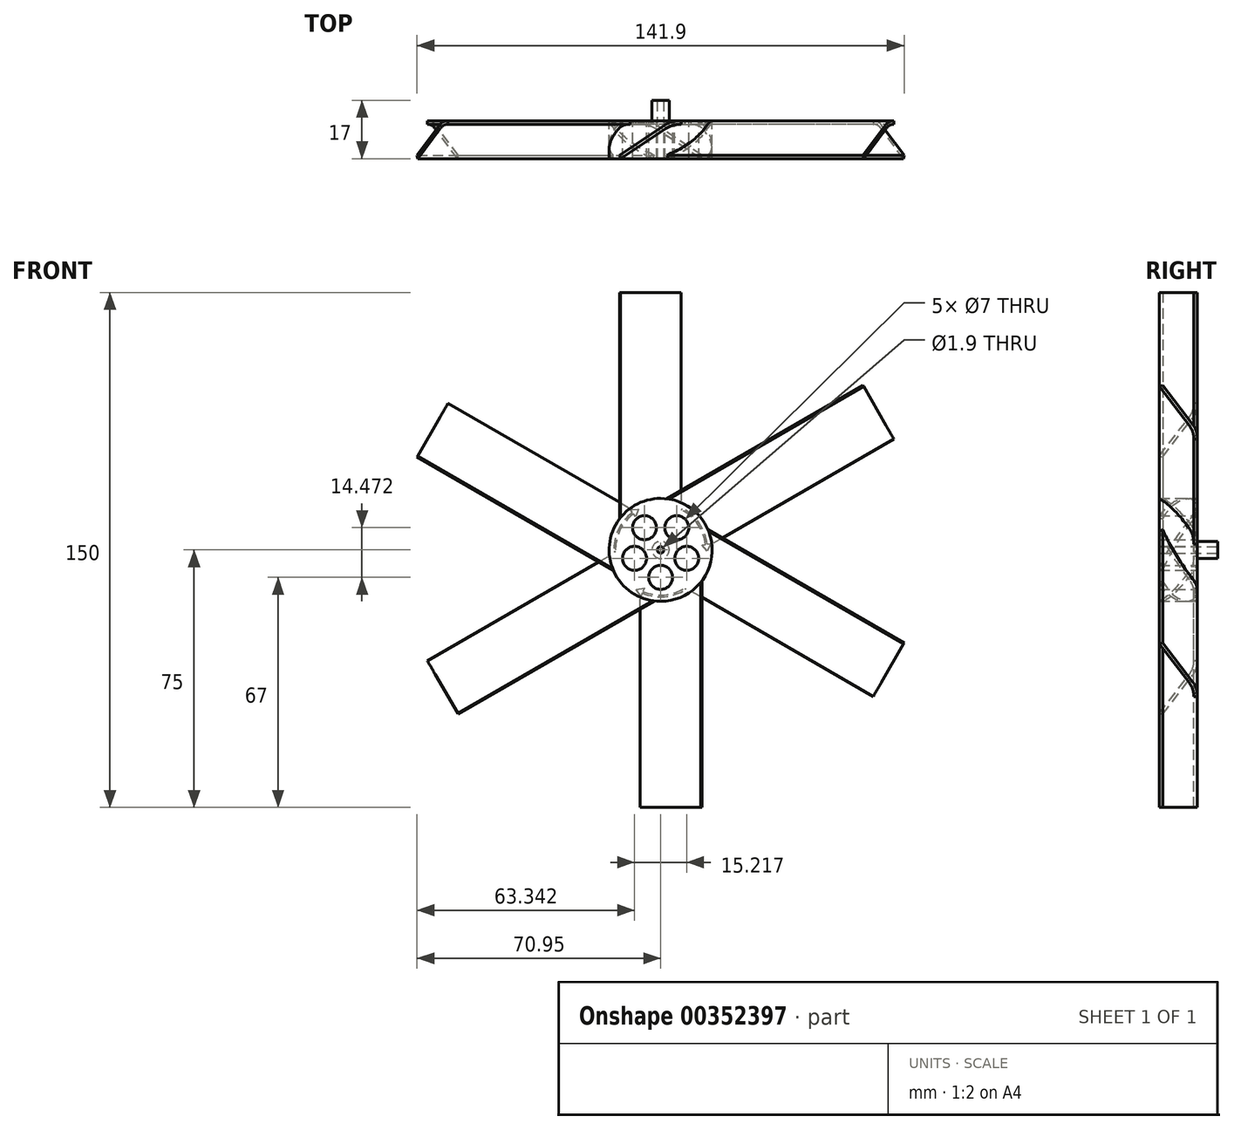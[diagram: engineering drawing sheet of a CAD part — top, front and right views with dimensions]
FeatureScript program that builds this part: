
annotation { "Feature Type Name" : "Feature", "Feature Type Description" : "" }
export const myFeature = defineFeature(function(context is Context, id is Id, definition is map)
    precondition{}
    {
        {
            var Q0;
            Q0=qCreatedBy(makeId("Top.planeOp"),FACE);
            var sketch = newSketch(context, id + "F0", { "sketchPlane" : qUnion([Q0])});
            skLineSegment(sketch, "E0", {"start": v(-3, 0) * mm, "end": v(12, 0) * mm, "construction": true});
            skLineSegment(sketch, "E1", {"start": v(12, 0) * mm, "end": v(12, -10) * mm, "construction": true});
            skLineSegment(sketch, "E2", {"start": v(12, -10) * mm, "end": v(-3, 0) * mm});
            skLineSegment(sketch, "E3.0", {"start": v(11.67, -10.98) * mm, "end": v(-3.33, -0.98) * mm});
            skLineSegment(sketch, "E4", {"start": v(11.67, -10.98) * mm, "end": v(12, -10) * mm});
            skLineSegment(sketch, "E5", {"start": v(-3, 0) * mm, "end": v(-3.33, -0.98) * mm});
            skLineSegment(sketch, "E6", {"start": v(-3, 0) * mm, "end": v(-6, 0) * mm});
            skLineSegment(sketch, "E7", {"start": v(-6, 0) * mm, "end": v(-6, -0.98) * mm});
            skLineSegment(sketch, "E8", {"start": v(-6, -0.98) * mm, "end": v(-3.33, -0.98) * mm});
            skSolve(sketch);
        }
        {
            var Q0;
            Q0=makeQuery(id+"F0.imprint","IMPRINT",FACE,{"disambiguationData":[TD([[makeQuery(id+"F0.imprint","IMPRINT",EDGE,{"derivedFrom":sQuery(id+"F0.wireOp",EDGE,"E2")}),1.0]])]});
            var Q1;
            Q1=makeQuery(id+"F0.imprint","IMPRINT",FACE,{"disambiguationData":[TD([[makeQuery(id+"F0.imprint","IMPRINT",EDGE,{"derivedFrom":sQuery(id+"F0.wireOp",EDGE,"E5")}),-1.0]])]});
            extrude(context, id + "F1", {"entities" : qUnion([Q0, Q1]), "oppositeDirection" : true, "depth" : 75 * mm});
        }
        {
            var Q0;
            Q0=makeQuery(id+"F1.opExtrude","SWEPT_EDGE",EDGE,{"disambiguationData":[OSD([sQuery(id+"F0.wireOp",EDGE,"E3.0"),sQuery(id+"F0.wireOp",EDGE,"E5"),sQuery(id+"F0.wireOp",EDGE,"E8")])]});
            var Q1;
            Q1=makeQuery(id+"F1.opExtrude","SWEPT_EDGE",EDGE,{"disambiguationData":[OSD([sQuery(id+"F0.wireOp",EDGE,"E2"),sQuery(id+"F0.wireOp",EDGE,"E5"),sQuery(id+"F0.wireOp",EDGE,"E6")])]});
            fillet(context, id + "F2", {"entities" : qUnion([Q0, Q1]), "radius" : 7.64 * mm, "tangentPropagation" : true, "allowEdgeOverflow" : false});
        }
        {
            var Q0;
            Q0=qCreatedBy(makeId("Top.planeOp"),FACE);
            var sketch = newSketch(context, id + "F3", { "sketchPlane" : qUnion([Q0])});
            skLineSegment(sketch, "E9", {"start": v(0, 0) * mm, "end": v(0, 27.05) * mm, "construction": true});
            skSolve(sketch);
        }
        {
            var Q0;
            Q0=makeQuery(id+"F1.opExtrude","SWEPT_BODY",BODY,{"disambiguationData":[OSD([sQuery(id+"F0.wireOp",EDGE,"E2"),sQuery(id+"F0.wireOp",EDGE,"E3.0"),sQuery(id+"F0.wireOp",EDGE,"E4"),sQuery(id+"F0.wireOp",EDGE,"E5")])]});
            var Q1;
            Q1=sQuery(id+"F3.wireOp",EDGE,"E9");
            circularPattern(context, id + "F4", {"entities" : qUnion([Q0]), "axis" : qUnion([Q1]), "angle" : 360 * degree, "instanceCount" : 6, "equalSpace" : true});
        }
        {
            var Q0;
            Q0=qCreatedBy(makeId("Front.planeOp"),FACE);
            var sketch = newSketch(context, id + "F5", { "sketchPlane" : qUnion([Q0])});
            skCircle(sketch, "E10", {"center": v(0, 0) * mm, "radius": 15 * mm});
            skSolve(sketch);
        }
        {
            var Q0;
            Q0=makeQuery(id+"F5.imprint","IMPRINT",FACE,{"disambiguationData":[TD([[makeQuery(id+"F5.imprint","IMPRINT",EDGE,{"derivedFrom":sQuery(id+"F5.wireOp",EDGE,"E10")}),1.0]])]});
            extrude(context, id + "F6", {"entities" : qUnion([Q0]), "operationType" : NewBodyOperationType.ADD, "depth" : 11 * mm});
        }
        {
            var Q0;
            Q0=makeQuery(id+"F6.opExtrude","CAP_FACE",FACE,{"disambiguationData":[OSD([sQuery(id+"F5.wireOp",EDGE,"E10")])],"isStart":true});
            var sketch = newSketch(context, id + "F7", { "sketchPlane" : qUnion([Q0])});
            skCircle(sketch, "E11", {"center": v(0, 0) * mm, "radius": 0.95 * mm});
            skLineSegment(sketch, "E12", {"start": v(0, 0) * mm, "end": v(-0.95, 0) * mm, "construction": true});
            skCircle(sketch, "E13", {"center": v(0, -8) * mm, "radius": 3.5 * mm});
            skCircle(sketch, "E14.1.0", {"center": v(7.6, -2.47) * mm, "radius": 3.5 * mm});
            skCircle(sketch, "E14.2.0", {"center": v(4.7, 6.47) * mm, "radius": 3.5 * mm});
            skCircle(sketch, "E14.3.0", {"center": v(-4.7, 6.47) * mm, "radius": 3.5 * mm});
            skCircle(sketch, "E14.4.0", {"center": v(-7.6, -2.47) * mm, "radius": 3.5 * mm});
            skSolve(sketch);
        }
        {
            var Q0;
            Q0=makeQuery(id+"F7.imprint","IMPRINT",FACE,{"disambiguationData":[TD([[makeQuery(id+"F7.imprint","IMPRINT",EDGE,{"derivedFrom":sQuery(id+"F7.wireOp",EDGE,"E14.3.0")}),1.0]])]});
            var Q1;
            Q1=makeQuery(id+"F7.imprint","IMPRINT",FACE,{"disambiguationData":[TD([[makeQuery(id+"F7.imprint","IMPRINT",EDGE,{"derivedFrom":sQuery(id+"F7.wireOp",EDGE,"E14.4.0")}),1.0]])]});
            var Q2;
            Q2=makeQuery(id+"F7.imprint","IMPRINT",FACE,{"disambiguationData":[TD([[makeQuery(id+"F7.imprint","IMPRINT",EDGE,{"derivedFrom":sQuery(id+"F7.wireOp",EDGE,"E13")}),1.0]])]});
            var Q3;
            Q3=makeQuery(id+"F7.imprint","IMPRINT",FACE,{"disambiguationData":[TD([[makeQuery(id+"F7.imprint","IMPRINT",EDGE,{"derivedFrom":sQuery(id+"F7.wireOp",EDGE,"E14.1.0")}),1.0]])]});
            var Q4;
            Q4=makeQuery(id+"F7.imprint","IMPRINT",FACE,{"disambiguationData":[TD([[makeQuery(id+"F7.imprint","IMPRINT",EDGE,{"derivedFrom":sQuery(id+"F7.wireOp",EDGE,"E14.2.0")}),1.0]])]});
            var Q5;
            Q5=makeQuery(id+"F7.imprint","IMPRINT",FACE,{"disambiguationData":[TD([[makeQuery(id+"F7.imprint","IMPRINT",EDGE,{"derivedFrom":sQuery(id+"F7.wireOp",EDGE,"E11")}),1.0]])]});
            extrude(context, id + "F8", {"entities" : qUnion([Q0, Q1, Q2, Q3, Q4, Q5]), "operationType" : NewBodyOperationType.REMOVE, "oppositeDirection" : true, "depth" : 25 * mm});
        }
        {
            var Q0;
            Q0=makeQuery(id+"F6.opExtrude","CAP_FACE",FACE,{"disambiguationData":[OSD([sQuery(id+"F5.wireOp",EDGE,"E10")])],"isStart":true});
            var sketch = newSketch(context, id + "F9", { "sketchPlane" : qUnion([Q0])});
            skArc(sketch, "E15", {"start": v(-7.05, -11.11) * mm, "mid": v(-1.07, -13.11) * mm, "end": v(5.16, -12.1) * mm});
            skArc(sketch, "E16.0", {"start": v(-7.29, -11.55) * mm, "mid": v(-1.1, -13.61) * mm, "end": v(5.35, -12.56) * mm});
            skLineSegment(sketch, "E17", {"start": v(-7.05, -11.11) * mm, "end": v(-7.29, -11.55) * mm});
            skLineSegment(sketch, "E18", {"start": v(5.35, -12.56) * mm, "end": v(5.75, -13.48) * mm});
            skLineSegment(sketch, "E19", {"start": v(5.75, -13.48) * mm, "end": v(7.1, -11.55) * mm});
            skLineSegment(sketch, "E20", {"start": v(7.1, -11.55) * mm, "end": v(4.77, -11.18) * mm});
            skLineSegment(sketch, "E21", {"start": v(4.77, -11.18) * mm, "end": v(5.16, -12.1) * mm});
            skLineSegment(sketch, "E22", {"start": v(5.35, -12.56) * mm, "end": v(5.16, -12.1) * mm, "construction": true});
            skLineSegment(sketch, "E23", {"start": v(5.26, -12.33) * mm, "end": v(7.1, -11.55) * mm, "construction": true});
            skLineSegment(sketch, "E24.1.0", {"start": v(6.45, 11.92) * mm, "end": v(7.3, 9.72) * mm});
            skLineSegment(sketch, "E24.1.1", {"start": v(7.3, 9.72) * mm, "end": v(7.9, 10.52) * mm});
            skLineSegment(sketch, "E24.1.2", {"start": v(8.8, 11.72) * mm, "end": v(6.45, 11.92) * mm});
            skArc(sketch, "E24.1.3", {"start": v(13.15, -0.55) * mm, "mid": v(11.9, 5.63) * mm, "end": v(7.9, 10.52) * mm});
            skArc(sketch, "E24.1.4", {"start": v(13.65, -0.54) * mm, "mid": v(12.34, 5.86) * mm, "end": v(8.2, 10.92) * mm});
            skLineSegment(sketch, "E24.1.5", {"start": v(8.2, 10.92) * mm, "end": v(8.8, 11.72) * mm});
            skLineSegment(sketch, "E24.1.6", {"start": v(8.05, 10.72) * mm, "end": v(6.45, 11.92) * mm, "construction": true});
            skLineSegment(sketch, "E24.1.7", {"start": v(13.15, -0.55) * mm, "end": v(13.65, -0.54) * mm});
            skLineSegment(sketch, "E24.1.8", {"start": v(8.2, 10.92) * mm, "end": v(7.9, 10.52) * mm, "construction": true});
            skLineSegment(sketch, "E24.2.0", {"start": v(-13.55, -0.37) * mm, "end": v(-12.07, 1.46) * mm});
            skLineSegment(sketch, "E24.2.1", {"start": v(-12.07, 1.46) * mm, "end": v(-13.06, 1.58) * mm});
            skLineSegment(sketch, "E24.2.2", {"start": v(-14.55, 1.77) * mm, "end": v(-13.55, -0.37) * mm});
            skArc(sketch, "E24.2.3", {"start": v(-6.1, 11.66) * mm, "mid": v(-10.82, 7.48) * mm, "end": v(-13.06, 1.58) * mm});
            skArc(sketch, "E24.2.4", {"start": v(-6.36, 12.09) * mm, "mid": v(-11.24, 7.75) * mm, "end": v(-13.56, 1.64) * mm});
            skLineSegment(sketch, "E24.2.5", {"start": v(-13.56, 1.64) * mm, "end": v(-14.55, 1.77) * mm});
            skLineSegment(sketch, "E24.2.6", {"start": v(-13.3, 1.61) * mm, "end": v(-13.55, -0.37) * mm, "construction": true});
            skLineSegment(sketch, "E24.2.7", {"start": v(-6.1, 11.66) * mm, "end": v(-6.36, 12.09) * mm});
            skLineSegment(sketch, "E24.2.8", {"start": v(-13.56, 1.64) * mm, "end": v(-13.06, 1.58) * mm, "construction": true});
            skSolve(sketch);
        }
        {
            var Q0;
            Q0=makeQuery(id+"F9.imprint","IMPRINT",FACE,{"disambiguationData":[TD([[makeQuery(id+"F9.imprint","IMPRINT",EDGE,{"derivedFrom":sQuery(id+"F9.wireOp",EDGE,"E15")}),-1.0]])]});
            var Q1;
            Q1=makeQuery(id+"F9.imprint","IMPRINT",FACE,{"disambiguationData":[TD([[makeQuery(id+"F9.imprint","IMPRINT",EDGE,{"derivedFrom":sQuery(id+"F9.wireOp",EDGE,"E24.1.0")}),1.0]])]});
            var Q2;
            Q2=makeQuery(id+"F9.imprint","IMPRINT",FACE,{"disambiguationData":[TD([[makeQuery(id+"F9.imprint","IMPRINT",EDGE,{"derivedFrom":sQuery(id+"F9.wireOp",EDGE,"E24.2.0")}),1.0]])]});
            extrude(context, id + "F10", {"entities" : qUnion([Q0, Q1, Q2]), "operationType" : NewBodyOperationType.REMOVE, "oppositeDirection" : true, "depth" : 1 * mm});
        }
        {
            var Q0;
            {var subQ0=makeQuery(id+"F1.opExtrude","SWEPT_FACE",FACE,{"disambiguationData":[OSD([sQuery(id+"F0.wireOp",EDGE,"E6")])]});Q0=makeQuery(id+"F6.boolean.opBoolean","MERGE",FACE,{"derivedFrom":[subQ0,makeQuery(id+"F4.opPattern","COPY",FACE,{"derivedFrom":subQ0,"instanceName":"1"}),makeQuery(id+"F4.opPattern","COPY",FACE,{"derivedFrom":subQ0,"instanceName":"2"}),makeQuery(id+"F4.opPattern","COPY",FACE,{"derivedFrom":subQ0,"instanceName":"3"}),makeQuery(id+"F4.opPattern","COPY",FACE,{"derivedFrom":subQ0,"instanceName":"4"}),makeQuery(id+"F4.opPattern","COPY",FACE,{"derivedFrom":subQ0,"instanceName":"5"}),makeQuery(id+"F6.opExtrude","CAP_FACE",FACE,{"disambiguationData":[OSD([sQuery(id+"F5.wireOp",EDGE,"E10")])],"isStart":true})]});}
            var sketch = newSketch(context, id + "F11", { "sketchPlane" : qUnion([Q0])});
            skCircle(sketch, "E25", {"center": v(0, 0) * mm, "radius": 2.5 * mm});
            skCircle(sketch, "E26.0", {"center": v(0, 0) * mm, "radius": 0.95 * mm});
            skSolve(sketch);
        }
        {
            var Q0;
            Q0=makeQuery(id+"F11.imprint","IMPRINT",FACE,{"disambiguationData":[TD([[makeQuery(id+"F11.imprint","IMPRINT",EDGE,{"derivedFrom":sQuery(id+"F11.wireOp",EDGE,"E25")}),1.0]])]});
            extrude(context, id + "F12", {"entities" : qUnion([Q0]), "operationType" : NewBodyOperationType.ADD, "depth" : 6 * mm});
        }
    });
